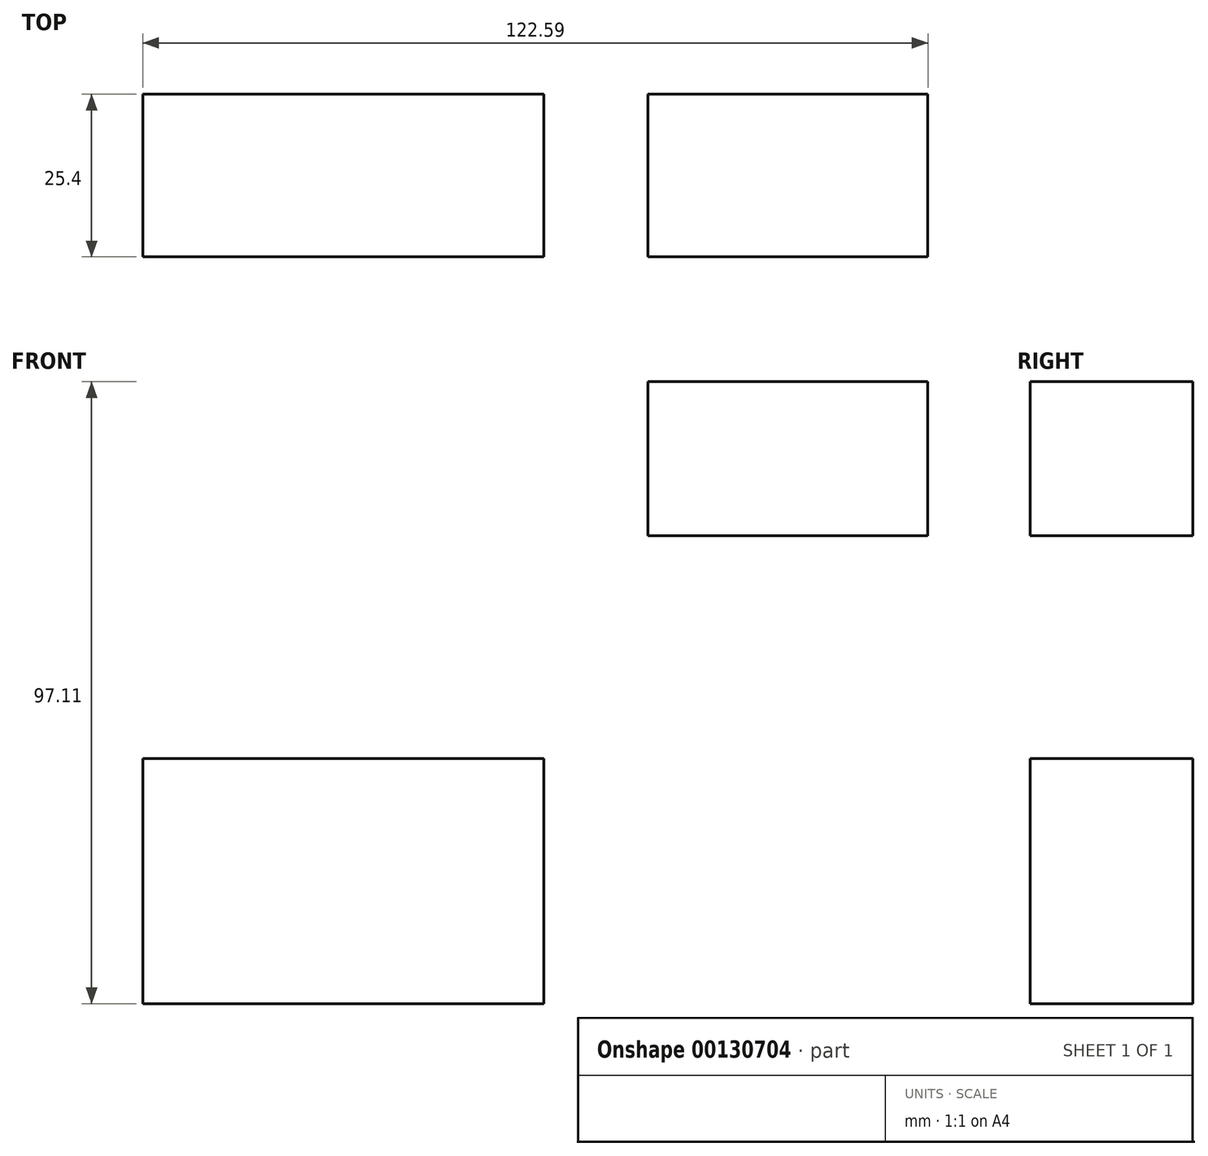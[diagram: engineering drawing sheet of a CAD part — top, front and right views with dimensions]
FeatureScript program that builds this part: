
annotation { "Feature Type Name" : "Feature", "Feature Type Description" : "" }
export const myFeature = defineFeature(function(context is Context, id is Id, definition is map)
    precondition{}
    {
        {
            var Q0;
            Q0=qCreatedBy(makeId("Front.planeOp"),FACE);
            var sketch = newSketch(context, id + "F0", { "sketchPlane" : qUnion([Q0])});
            skLineSegment(sketch, "E0.bottom", {"start": v(-31.31, 19.14) * mm, "end": v(31.31, 19.14) * mm});
            skLineSegment(sketch, "E0.top", {"start": v(-31.31, -19.14) * mm, "end": v(31.31, -19.14) * mm});
            skLineSegment(sketch, "E0.left", {"start": v(-31.31, 19.14) * mm, "end": v(-31.31, -19.14) * mm});
            skLineSegment(sketch, "E0.right", {"start": v(31.31, 19.14) * mm, "end": v(31.31, -19.14) * mm});
            skPoint(sketch, "E0.middle", {"position": v(0, 0) * mm});
            skLineSegment(sketch, "E1.bottom", {"start": v(91.28, 77.97) * mm, "end": v(47.54, 77.97) * mm});
            skLineSegment(sketch, "E1.top", {"start": v(91.28, 53.95) * mm, "end": v(47.54, 53.95) * mm});
            skLineSegment(sketch, "E1.left", {"start": v(91.28, 77.97) * mm, "end": v(91.28, 53.95) * mm});
            skLineSegment(sketch, "E1.right", {"start": v(47.54, 77.97) * mm, "end": v(47.54, 53.95) * mm});
            skLineSegment(sketch, "E2", {"start": v(15.2, 13.6) * mm, "end": v(15.2, 42.86) * mm});
            skLineSegment(sketch, "E3", {"start": v(-2.97, 14.52) * mm, "end": v(-2.97, 32.38) * mm});
            skArc(sketch, "E4", {"start": v(15.2, 42.86) * mm, "mid": v(26.01, 61.48) * mm, "end": v(47.54, 61.34) * mm});
            skArc(sketch, "E5", {"start": v(-2.97, 32.38) * mm, "mid": v(13.29, 62.7) * mm, "end": v(47.54, 65.96) * mm});
            skSolve(sketch);
        }
        {
            var Q0;
            {var subQ1=sQuery(id+"F0.wireOp",EDGE,"E1.bottom");Q0=makeQuery(id+"F0.imprint","IMPRINT",FACE,{"disambiguationData":[TD([[makeQuery(id+"F0.imprint","IMPRINT",EDGE,{"derivedFrom":subQ1}),1.0]])]});}
            var Q1;
            {var subQ4=sQuery(id+"F0.wireOp",EDGE,"E4");Q1=makeQuery(id+"F0.imprint","IMPRINT",FACE,{"disambiguationData":[TD([[makeQuery(id+"F0.imprint","IMPRINT",EDGE,{"derivedFrom":subQ4}),1.0]])]});}
            var Q2;
            Q2=makeQuery(id+"F0.imprint","IMPRINT",FACE,{"disambiguationData":[TD([[makeQuery(id+"F0.imprint","IMPRINT",EDGE,{"derivedFrom":sQuery(id+"F0.wireOp",EDGE,"E0.top")}),1.0]])]});
            extrude(context, id + "F1", {"entities" : qUnion([Q0, Q1, Q2]), "depth" : 25.4 * mm});
        }
    });
